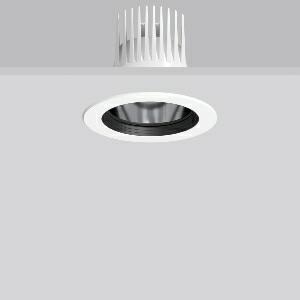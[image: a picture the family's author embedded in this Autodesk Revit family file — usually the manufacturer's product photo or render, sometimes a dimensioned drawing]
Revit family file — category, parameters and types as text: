
# Revit family: heledon_maxi_e_901759_002_1_76_e72b
name_source: partatom
category: Lighting Fixtures
units: mm (PartAtom-declared; Revit-internal decimal feet)

## family parameters
Cut with Voids When Loaded = No
Host = Face
Light Source = No
Part Type = Normal
Room Calculation Point = No
Round Connector Dimension = Use Diameter
Shared = No

## types (1)
- HELEDON maxi E (1 x LED Modul 940, 3350 lm, 4000)
    Apparent Load = 25 VA
    Approval mark = CE
    CIE Flux Codes = 97 100 100 100 100
    Color Rendering = 92
    Color Temperature = 4000
    Default Elevation = 1800 mm
    Description = Series: HELEDON maxi
Round recessed downlight. Housing: die-cast aluminium, powder-coated. Black plastic ring and recessed LED to prevent glare from the side. Optical assembly with reflector made of MIRO-Silver with 98% total light reflection for outstanding efficiency - can be changed without tools. Best colour rendering index Ra>90. Suitable for Recessed ceiling mounting. Installation without tools thanks to spring fastening system. Including separate LED converter with connecting cable 600 mm.High quality converter without flickering and stroboscopic effect. Through-wiring box (5 pole) available as accessory. The following accessories can be mounted without use of tools: interchangeable lenses, decorative glasses, honeycomb louvre, clear and frosted diffusers, white interchangeable plastic ring. 
Colour: traffic white, matt (RAL 9016)
Diameter: 162 mm
Height: 3 mm
Cut-out diameter: 152 mm
Recess height: 200 mm
Luminaire: recess height: 135 mm
Lamp: LED
Socket: without socket
Colour temperature: 4000K
Colour rendering index (CRI): 92
System power: 25 W
Rated luminous flux: 3350 lm
Luminous efficiency: 134 lm/W
Control gear: Converter, dimmable, DALI
Protection class: II
Type of protection: IP 20
    Height = 0 mm  [stored 0 ft]
    Lamp = 1 x LED Modul 940
    Lamp Light Flux = 3350 lm
    Lamp count = 1
    Length = 162 mm
    Lifetime = 50000 h
    Luminous efficacy = 134 lm/W
    Manufacturer = RZB
    ModVariant = No
    Model = 901759.002.1.76
    Mounting Place = Ceiling
    Mounting Type = Recessed
    Number of Poles = 1
    OnlyDefault = Yes
    Power Factor = 1
    Product Name = HELEDON maxi E
    Product group = Recessed downlights
    ProductGroupID = 402
    Protection Class = Protection class II
    Protection Degree = IP 20
    RLX_Detail_Level = 1
    RLX_Emergency_Light_Flux = 0 lm
    RLX_Emergency_Type = 0
    RLX_Emergency_Type_DB = No
    RlxData = <blob elided: 118957 chars, md5=1f71e358>
    Socket = socket
    Standby Power = 0 W
    System Light Flux = 3350 lm
    System Power = 25 W
    Type Comments = Product without accessories
    Type Image = 901662.002.jpg
    URL = http://relux.com
    VarID = ---
    Voltage = 230 V
    Voltage Range = 220-240 V
    Weight = 0.00 kg
    Width = 0 mm  [stored 0 ft]

note: [stored X ft] marks values corroborated as IEEE doubles in the binary element streams (Revit-internal decimal feet)

## geometry (parser evidence)
native form markers: Blend x4, Sweep x12
no freeform markers — native parametric forms only
